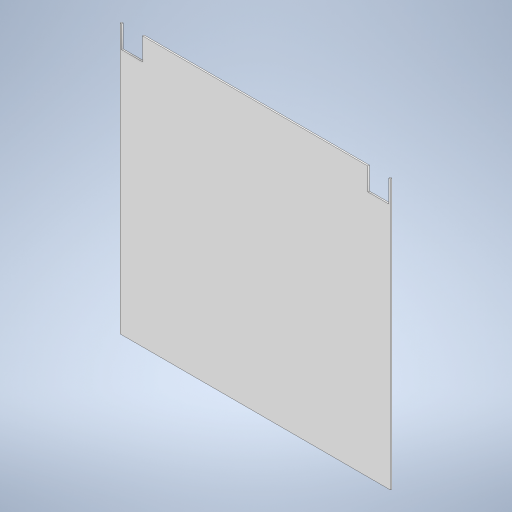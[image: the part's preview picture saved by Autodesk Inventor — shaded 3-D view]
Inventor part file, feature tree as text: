
AUTODESK INVENTOR PART (.ipt)
format: ipt  version: 2023 (Build 270158000, 158)  size: 214,528 bytes
history: native  units: mm
features: extrude x1
ambient origin geometry x8: Origin, YZ Plane, XZ Plane, XY Plane, X Axis, Y Axis, Z Axis, Center Point
bodies: Solid1 (feature_tree)
feature tree (1):
  extrude  "Extrusion1"  Depth=542.0mm
